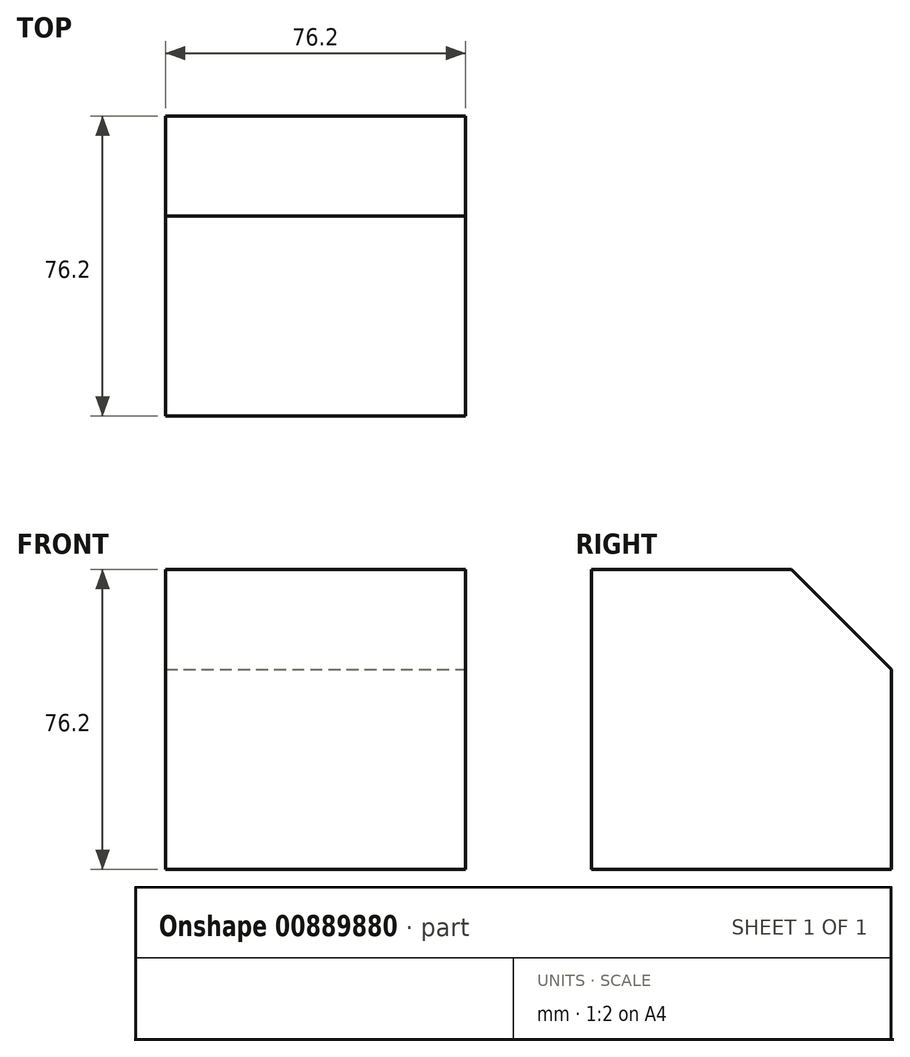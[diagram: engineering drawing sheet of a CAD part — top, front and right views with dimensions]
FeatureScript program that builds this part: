
annotation { "Feature Type Name" : "Feature", "Feature Type Description" : "" }
export const myFeature = defineFeature(function(context is Context, id is Id, definition is map)
    precondition{}
    {
        {
            var Q0;
            Q0=qCreatedBy(makeId("Top.planeOp"),FACE);
            var sketch = newSketch(context, id + "F0", { "sketchPlane" : qUnion([Q0])});
            skLineSegment(sketch, "E0.bottom", {"start": v(38.1, 38.1) * mm, "end": v(-38.1, 38.1) * mm});
            skLineSegment(sketch, "E0.top", {"start": v(38.1, -38.1) * mm, "end": v(-38.1, -38.1) * mm});
            skLineSegment(sketch, "E0.left", {"start": v(38.1, 38.1) * mm, "end": v(38.1, -38.1) * mm});
            skLineSegment(sketch, "E0.right", {"start": v(-38.1, 38.1) * mm, "end": v(-38.1, -38.1) * mm});
            skPoint(sketch, "E0.middle", {"position": v(0, 0) * mm});
            skSolve(sketch);
        }
        {
            var Q0;
            Q0=makeQuery(id+"F0.imprint","IMPRINT",FACE,{"disambiguationData":[TD([[makeQuery(id+"F0.imprint","IMPRINT",EDGE,{"derivedFrom":sQuery(id+"F0.wireOp",EDGE,"E0.bottom")}),1.0]])]});
            extrude(context, id + "F1", {"entities" : qUnion([Q0]), "depth" : 76.2 * mm, "offsetDistance" : 25.4 * mm});
        }
        {
            var Q0;
            Q0=makeQuery(id+"F1.opExtrude","SWEPT_FACE",FACE,{"disambiguationData":[OSD([sQuery(id+"F0.wireOp",EDGE,"E0.left")])]});
            var sketch = newSketch(context, id + "F2", { "sketchPlane" : qUnion([Q0])});
            skLineSegment(sketch, "E1", {"start": v(12.7, 76.2) * mm, "end": v(38.1, 50.8) * mm});
            skLineSegment(sketch, "E2", {"start": v(38.1, 50.8) * mm, "end": v(38.1, 76.2) * mm});
            skLineSegment(sketch, "E3", {"start": v(38.1, 76.2) * mm, "end": v(12.7, 76.2) * mm});
            skSolve(sketch);
        }
        {
            var Q0;
            Q0=makeQuery(id+"F2.imprint","IMPRINT",FACE,{"disambiguationData":[TD([[makeQuery(id+"F2.imprint","IMPRINT",EDGE,{"derivedFrom":sQuery(id+"F2.wireOp",EDGE,"E1")}),1.0]])]});
            extrude(context, id + "F3", {"entities" : qUnion([Q0]), "operationType" : NewBodyOperationType.REMOVE, "endBound" : BoundingType.THROUGH_ALL, "oppositeDirection" : true, "depth" : 25.4 * mm, "offsetDistance" : 25.4 * mm});
        }
    });
